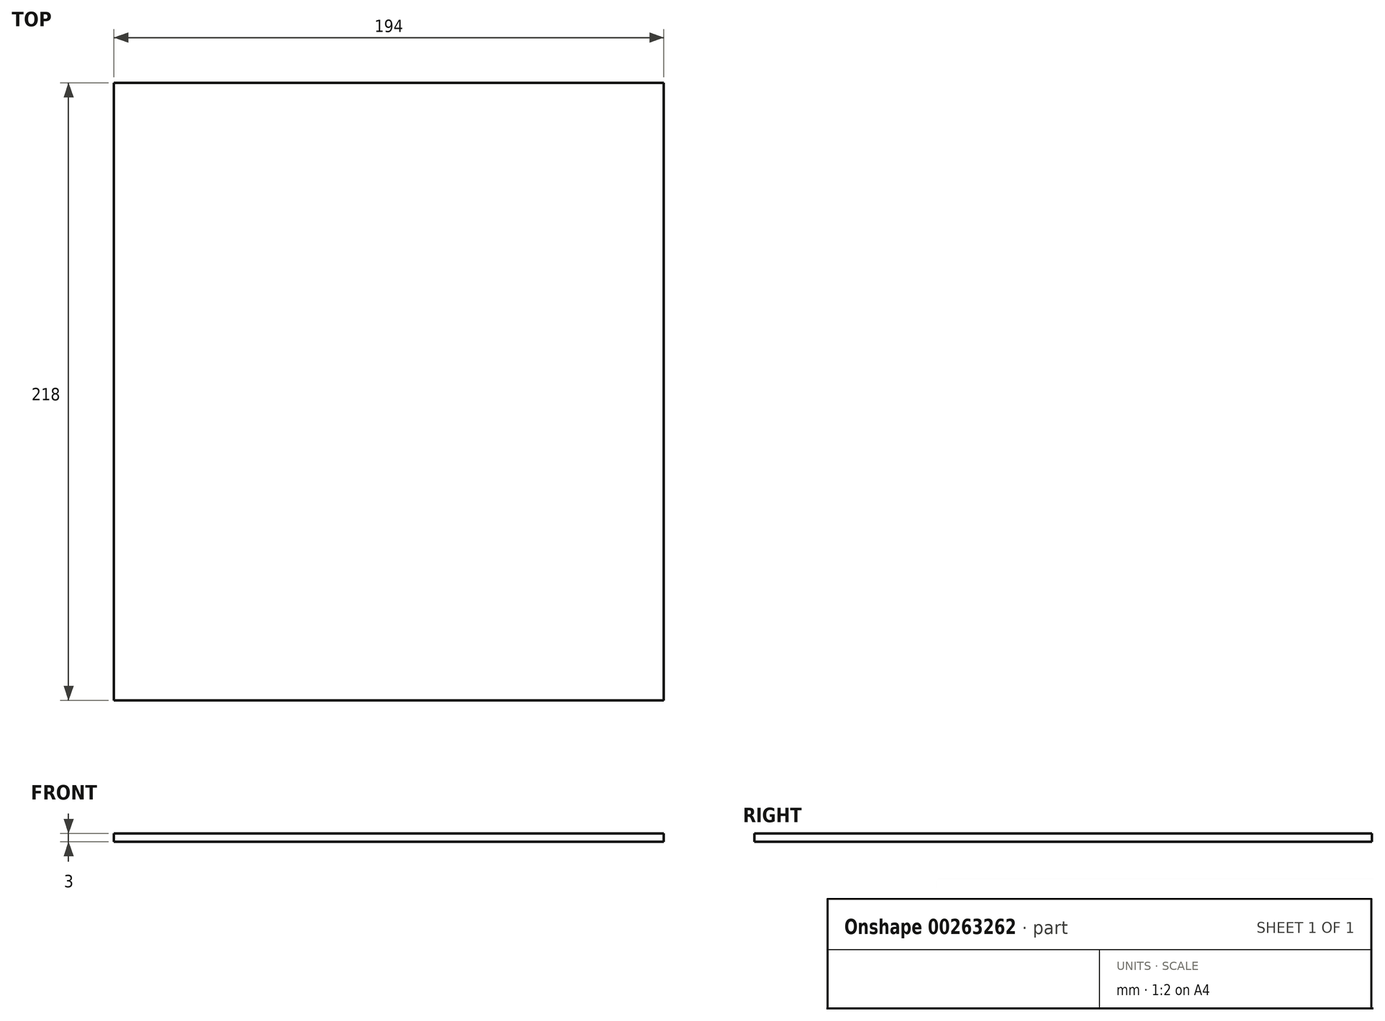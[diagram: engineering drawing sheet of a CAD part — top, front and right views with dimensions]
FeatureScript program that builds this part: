
annotation { "Feature Type Name" : "Feature", "Feature Type Description" : "" }
export const myFeature = defineFeature(function(context is Context, id is Id, definition is map)
    precondition{}
    {
        {
            var Q0;
            Q0=qCreatedBy(makeId("Top.planeOp"),FACE);
            var sketch = newSketch(context, id + "F0", { "sketchPlane" : qUnion([Q0])});
            skLineSegment(sketch, "E0.bottom", {"start": v(97, -109) * mm, "end": v(-97, -109) * mm});
            skLineSegment(sketch, "E0.top", {"start": v(97, 109) * mm, "end": v(-97, 109) * mm});
            skLineSegment(sketch, "E0.left", {"start": v(97, -109) * mm, "end": v(97, 109) * mm});
            skLineSegment(sketch, "E0.right", {"start": v(-97, -109) * mm, "end": v(-97, 109) * mm});
            skPoint(sketch, "E0.middle", {"position": v(0, 0) * mm});
            skSolve(sketch);
        }
        {
            var Q0;
            Q0 = qSketchRegion(id + "F0", true);
            extrude(context, id + "F1", {"entities" : qUnion([Q0]), "depth" : 3 * mm});
        }
    });
